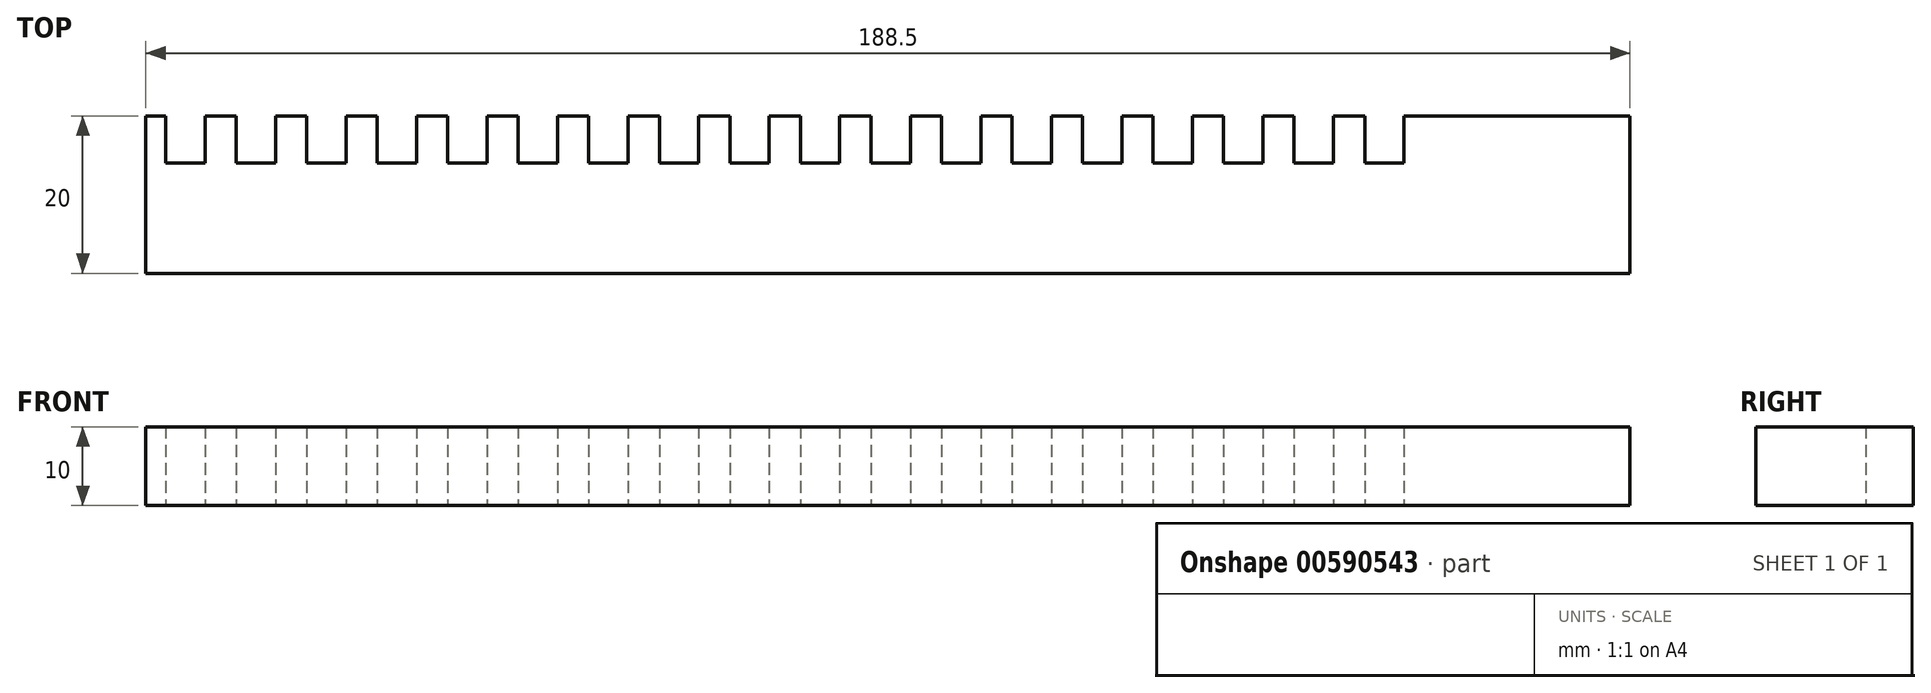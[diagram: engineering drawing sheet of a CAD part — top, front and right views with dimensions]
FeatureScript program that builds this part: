
annotation { "Feature Type Name" : "Feature", "Feature Type Description" : "" }
export const myFeature = defineFeature(function(context is Context, id is Id, definition is map)
    precondition{}
    {
        {
            var Q0;
            Q0=qCreatedBy(makeId("Top.planeOp"),FACE);
            var sketch = newSketch(context, id + "F0", { "sketchPlane" : qUnion([Q0])});
            skLineSegment(sketch, "E0.bottom", {"start": v(0, 0) * mm, "end": v(188.5, 0) * mm});
            skLineSegment(sketch, "E0.top", {"start": v(0, 20) * mm, "end": v(2.5, 20) * mm});
            skLineSegment(sketch, "E0.left", {"start": v(0, 0) * mm, "end": v(0, 20) * mm});
            skLineSegment(sketch, "E0.right", {"start": v(188.5, 0) * mm, "end": v(188.5, 20) * mm});
            skPoint(sketch, "E1", {"position": v(5, 20) * mm});
            skLineSegment(sketch, "E2", {"start": v(5, 14) * mm, "end": v(2.5, 14) * mm});
            skLineSegment(sketch, "E3", {"start": v(2.5, 14) * mm, "end": v(2.5, 20) * mm});
            skLineSegment(sketch, "E4.MirrorCS", {"start": v(7.5, 14) * mm, "end": v(7.5, 20) * mm});
            skLineSegment(sketch, "E5.MirrorCS", {"start": v(5, 14) * mm, "end": v(7.5, 14) * mm});
            skLineSegment(sketch, "E6.trimOffspring", {"start": v(7.5, 20) * mm, "end": v(11.46, 20) * mm});
            skLineSegment(sketch, "E7.1.0.0", {"start": v(16.46, 14) * mm, "end": v(16.46, 20) * mm});
            skLineSegment(sketch, "E7.1.0.1", {"start": v(13.96, 14) * mm, "end": v(16.46, 14) * mm});
            skLineSegment(sketch, "E7.1.0.2", {"start": v(13.96, 14) * mm, "end": v(11.46, 14) * mm});
            skLineSegment(sketch, "E7.1.0.3", {"start": v(11.46, 14) * mm, "end": v(11.46, 20) * mm});
            skLineSegment(sketch, "E7.2.0.0", {"start": v(25.42, 14) * mm, "end": v(25.42, 20) * mm});
            skLineSegment(sketch, "E7.2.0.1", {"start": v(22.92, 14) * mm, "end": v(25.42, 14) * mm});
            skLineSegment(sketch, "E7.2.0.2", {"start": v(22.92, 14) * mm, "end": v(20.42, 14) * mm});
            skLineSegment(sketch, "E7.2.0.3", {"start": v(20.42, 14) * mm, "end": v(20.42, 20) * mm});
            skLineSegment(sketch, "E7.3.0.0", {"start": v(34.38, 14) * mm, "end": v(34.38, 20) * mm});
            skLineSegment(sketch, "E7.3.0.1", {"start": v(31.88, 14) * mm, "end": v(34.38, 14) * mm});
            skLineSegment(sketch, "E7.3.0.2", {"start": v(31.88, 14) * mm, "end": v(29.38, 14) * mm});
            skLineSegment(sketch, "E7.3.0.3", {"start": v(29.38, 14) * mm, "end": v(29.38, 20) * mm});
            skLineSegment(sketch, "E7.4.0.0", {"start": v(43.34, 14) * mm, "end": v(43.34, 20) * mm});
            skLineSegment(sketch, "E7.4.0.1", {"start": v(40.84, 14) * mm, "end": v(43.34, 14) * mm});
            skLineSegment(sketch, "E7.4.0.2", {"start": v(40.84, 14) * mm, "end": v(38.34, 14) * mm});
            skLineSegment(sketch, "E7.4.0.3", {"start": v(38.34, 14) * mm, "end": v(38.34, 20) * mm});
            skLineSegment(sketch, "E7.5.0.0", {"start": v(52.3, 14) * mm, "end": v(52.3, 20) * mm});
            skLineSegment(sketch, "E7.5.0.1", {"start": v(49.8, 14) * mm, "end": v(52.3, 14) * mm});
            skLineSegment(sketch, "E7.5.0.2", {"start": v(49.8, 14) * mm, "end": v(47.3, 14) * mm});
            skLineSegment(sketch, "E7.5.0.3", {"start": v(47.3, 14) * mm, "end": v(47.3, 20) * mm});
            skLineSegment(sketch, "E7.6.0.0", {"start": v(61.26, 14) * mm, "end": v(61.26, 20) * mm});
            skLineSegment(sketch, "E7.6.0.1", {"start": v(58.76, 14) * mm, "end": v(61.26, 14) * mm});
            skLineSegment(sketch, "E7.6.0.2", {"start": v(58.76, 14) * mm, "end": v(56.26, 14) * mm});
            skLineSegment(sketch, "E7.6.0.3", {"start": v(56.26, 14) * mm, "end": v(56.26, 20) * mm});
            skLineSegment(sketch, "E7.7.0.0", {"start": v(70.22, 14) * mm, "end": v(70.22, 20) * mm});
            skLineSegment(sketch, "E7.7.0.1", {"start": v(67.72, 14) * mm, "end": v(70.22, 14) * mm});
            skLineSegment(sketch, "E7.7.0.2", {"start": v(67.72, 14) * mm, "end": v(65.22, 14) * mm});
            skLineSegment(sketch, "E7.7.0.3", {"start": v(65.22, 14) * mm, "end": v(65.22, 20) * mm});
            skLineSegment(sketch, "E7.8.0.0", {"start": v(79.18, 14) * mm, "end": v(79.18, 20) * mm});
            skLineSegment(sketch, "E7.8.0.1", {"start": v(76.68, 14) * mm, "end": v(79.18, 14) * mm});
            skLineSegment(sketch, "E7.8.0.2", {"start": v(76.68, 14) * mm, "end": v(74.18, 14) * mm});
            skLineSegment(sketch, "E7.8.0.3", {"start": v(74.18, 14) * mm, "end": v(74.18, 20) * mm});
            skLineSegment(sketch, "E7.9.0.0", {"start": v(88.14, 14) * mm, "end": v(88.14, 20) * mm});
            skLineSegment(sketch, "E7.9.0.1", {"start": v(85.64, 14) * mm, "end": v(88.14, 14) * mm});
            skLineSegment(sketch, "E7.9.0.2", {"start": v(85.64, 14) * mm, "end": v(83.14, 14) * mm});
            skLineSegment(sketch, "E7.9.0.3", {"start": v(83.14, 14) * mm, "end": v(83.14, 20) * mm});
            skLineSegment(sketch, "E7.10.0.0", {"start": v(97.1, 14) * mm, "end": v(97.1, 20) * mm});
            skLineSegment(sketch, "E7.10.0.1", {"start": v(94.6, 14) * mm, "end": v(97.1, 14) * mm});
            skLineSegment(sketch, "E7.10.0.2", {"start": v(94.6, 14) * mm, "end": v(92.1, 14) * mm});
            skLineSegment(sketch, "E7.10.0.3", {"start": v(92.1, 14) * mm, "end": v(92.1, 20) * mm});
            skLineSegment(sketch, "E7.11.0.0", {"start": v(106.06, 14) * mm, "end": v(106.06, 20) * mm});
            skLineSegment(sketch, "E7.11.0.1", {"start": v(103.56, 14) * mm, "end": v(106.06, 14) * mm});
            skLineSegment(sketch, "E7.11.0.2", {"start": v(103.56, 14) * mm, "end": v(101.06, 14) * mm});
            skLineSegment(sketch, "E7.11.0.3", {"start": v(101.06, 14) * mm, "end": v(101.06, 20) * mm});
            skLineSegment(sketch, "E7.12.0.0", {"start": v(115.02, 14) * mm, "end": v(115.02, 20) * mm});
            skLineSegment(sketch, "E7.12.0.1", {"start": v(112.52, 14) * mm, "end": v(115.02, 14) * mm});
            skLineSegment(sketch, "E7.12.0.2", {"start": v(112.52, 14) * mm, "end": v(110.02, 14) * mm});
            skLineSegment(sketch, "E7.12.0.3", {"start": v(110.02, 14) * mm, "end": v(110.02, 20) * mm});
            skLineSegment(sketch, "E7.13.0.0", {"start": v(123.98, 14) * mm, "end": v(123.98, 20) * mm});
            skLineSegment(sketch, "E7.13.0.1", {"start": v(121.48, 14) * mm, "end": v(123.98, 14) * mm});
            skLineSegment(sketch, "E7.13.0.2", {"start": v(121.48, 14) * mm, "end": v(118.98, 14) * mm});
            skLineSegment(sketch, "E7.13.0.3", {"start": v(118.98, 14) * mm, "end": v(118.98, 20) * mm});
            skLineSegment(sketch, "E7.14.0.0", {"start": v(132.94, 14) * mm, "end": v(132.94, 20) * mm});
            skLineSegment(sketch, "E7.14.0.1", {"start": v(130.44, 14) * mm, "end": v(132.94, 14) * mm});
            skLineSegment(sketch, "E7.14.0.2", {"start": v(130.44, 14) * mm, "end": v(127.94, 14) * mm});
            skLineSegment(sketch, "E7.14.0.3", {"start": v(127.94, 14) * mm, "end": v(127.94, 20) * mm});
            skLineSegment(sketch, "E7.15.0.0", {"start": v(141.9, 14) * mm, "end": v(141.9, 20) * mm});
            skLineSegment(sketch, "E7.15.0.1", {"start": v(139.4, 14) * mm, "end": v(141.9, 14) * mm});
            skLineSegment(sketch, "E7.15.0.2", {"start": v(139.4, 14) * mm, "end": v(136.9, 14) * mm});
            skLineSegment(sketch, "E7.15.0.3", {"start": v(136.9, 14) * mm, "end": v(136.9, 20) * mm});
            skLineSegment(sketch, "E7.16.0.0", {"start": v(150.86, 14) * mm, "end": v(150.86, 20) * mm});
            skLineSegment(sketch, "E7.16.0.1", {"start": v(148.36, 14) * mm, "end": v(150.86, 14) * mm});
            skLineSegment(sketch, "E7.16.0.2", {"start": v(148.36, 14) * mm, "end": v(145.86, 14) * mm});
            skLineSegment(sketch, "E7.16.0.3", {"start": v(145.86, 14) * mm, "end": v(145.86, 20) * mm});
            skLineSegment(sketch, "E7.17.0.0", {"start": v(159.82, 14) * mm, "end": v(159.82, 20) * mm});
            skLineSegment(sketch, "E7.17.0.1", {"start": v(157.32, 14) * mm, "end": v(159.82, 14) * mm});
            skLineSegment(sketch, "E7.17.0.2", {"start": v(157.32, 14) * mm, "end": v(154.82, 14) * mm});
            skLineSegment(sketch, "E7.17.0.3", {"start": v(154.82, 14) * mm, "end": v(154.82, 20) * mm});
            skLineSegment(sketch, "E7.direction1", {"start": v(7.5, 14) * mm, "end": v(16.46, 14) * mm, "construction": true});
            skLineSegment(sketch, "E8.trimOffspring", {"start": v(16.46, 20) * mm, "end": v(20.42, 20) * mm});
            skLineSegment(sketch, "E9.trimOffspring", {"start": v(25.42, 20) * mm, "end": v(29.38, 20) * mm});
            skLineSegment(sketch, "E10.trimOffspring", {"start": v(34.38, 20) * mm, "end": v(38.34, 20) * mm});
            skLineSegment(sketch, "E11.trimOffspring", {"start": v(43.34, 20) * mm, "end": v(47.3, 20) * mm});
            skLineSegment(sketch, "E12.trimOffspring", {"start": v(52.3, 20) * mm, "end": v(56.26, 20) * mm});
            skLineSegment(sketch, "E13.trimOffspring", {"start": v(61.26, 20) * mm, "end": v(65.22, 20) * mm});
            skLineSegment(sketch, "E14.trimOffspring", {"start": v(70.22, 20) * mm, "end": v(188.5, 20) * mm});
            skSolve(sketch);
        }
        {
            var Q0;
            Q0=makeQuery(id+"F0.imprint","IMPRINT",FACE,{"disambiguationData":[TD([[makeQuery(id+"F0.imprint","IMPRINT",EDGE,{"derivedFrom":sQuery(id+"F0.wireOp",EDGE,"E0.bottom")}),1.0]])]});
            extrude(context, id + "F1", {"entities" : qUnion([Q0]), "depth" : 10 * mm, "offsetDistance" : 25 * mm});
        }
    });
